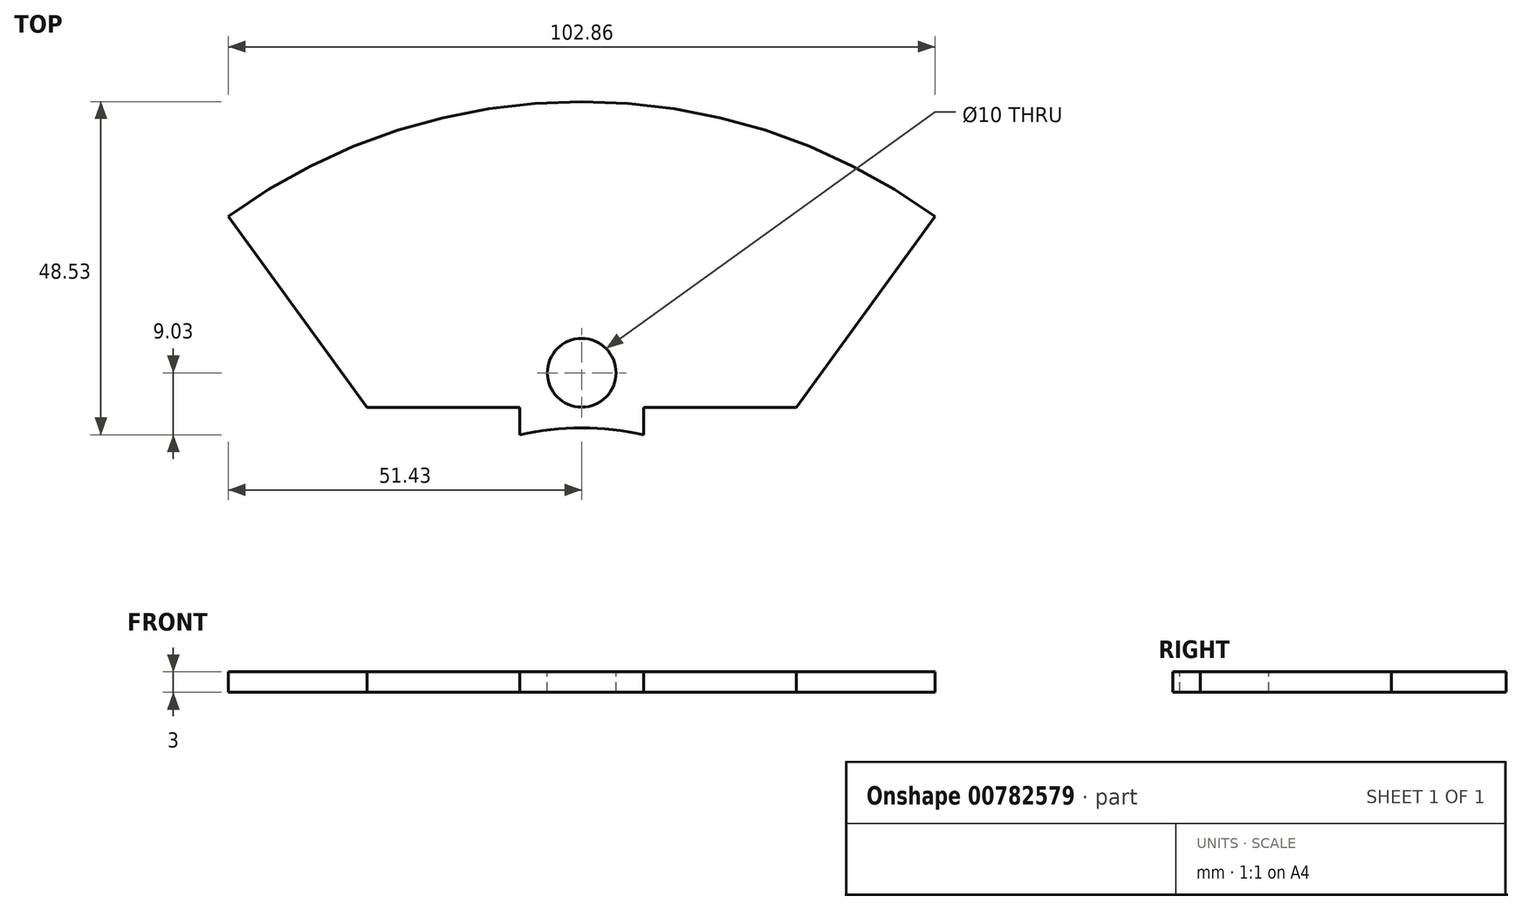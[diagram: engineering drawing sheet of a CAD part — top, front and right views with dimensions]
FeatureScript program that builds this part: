
annotation { "Feature Type Name" : "Feature", "Feature Type Description" : "" }
export const myFeature = defineFeature(function(context is Context, id is Id, definition is map)
    precondition{}
    {
        {
            var Q0;
            Q0=qCreatedBy(makeId("Top.planeOp"),FACE);
            var sketch = newSketch(context, id + "F0", { "sketchPlane" : qUnion([Q0])});
            skArc(sketch, "E0", {"start": v(51.43, 70.79) * mm, "mid": v(0, 87.5) * mm, "end": v(-51.43, 70.79) * mm});
            skLineSegment(sketch, "E1", {"start": v(0, 0) * mm, "end": v(104.27, 0) * mm, "construction": true});
            skLineSegment(sketch, "E2", {"start": v(0, 0) * mm, "end": v(-103.94, 0) * mm, "construction": true});
            skLineSegment(sketch, "E3", {"start": v(0, 0) * mm, "end": v(0, 97.04) * mm, "construction": true});
            skLineSegment(sketch, "E4", {"start": v(0, 0) * mm, "end": v(0, -125.2) * mm, "construction": true});
            skLineSegment(sketch, "E5", {"start": v(0, 0) * mm, "end": v(51.43, 70.79) * mm});
            skLineSegment(sketch, "E6.MirrorCS", {"start": v(0, 0) * mm, "end": v(-51.43, 70.79) * mm});
            skSolve(sketch);
        }
        {
            var Q0;
            Q0=makeQuery(id+"F0.imprint","IMPRINT",FACE,{"disambiguationData":[TD([[makeQuery(id+"F0.imprint","IMPRINT",EDGE,{"derivedFrom":sQuery(id+"F0.wireOp",EDGE,"E0")}),1.0]])]});
            extrude(context, id + "F1", {"entities" : qUnion([Q0]), "depth" : 3 * mm, "offsetDistance" : 25 * mm});
        }
        {
            var Q0;
            Q0=makeQuery(id+"F1.opExtrude","CAP_FACE",FACE,{"disambiguationData":[OSD([sQuery(id+"F0.wireOp",EDGE,"E0"),sQuery(id+"F0.wireOp",EDGE,"E5"),sQuery(id+"F0.wireOp",EDGE,"E6.MirrorCS")])],"isStart":false});
            var sketch = newSketch(context, id + "F2", { "sketchPlane" : qUnion([Q0])});
            skCircle(sketch, "E7", {"center": v(0, 0) * mm, "radius": 40 * mm});
            skSolve(sketch);
        }
        {
            var Q0;
            {var subQ0=sQuery(id+"F2.wireOp",EDGE,"E7");var subQ1=makeQuery(id+"F1.opExtrude","CAP_EDGE",EDGE,{"disambiguationData":[OSD([sQuery(id+"F0.wireOp",EDGE,"E5")])],"isStart":false});var subQ2=makeQuery(id+"F2.imprint","INTERSECT",VERTEX,{"derivedFrom":[subQ1,subQ0]});Q0=makeQuery(id+"F2.imprint","IMPRINT",FACE,{"disambiguationData":[TD([[makeQuery(id+"F2.imprint","IMPRINT",EDGE,{"disambiguationData":[TD([[subQ2,-1.0]])],"derivedFrom":subQ0}),1.0]])]});}
            extrude(context, id + "F3", {"entities" : qUnion([Q0]), "operationType" : NewBodyOperationType.REMOVE, "endBound" : BoundingType.THROUGH_ALL, "oppositeDirection" : true, "depth" : 25 * mm, "offsetDistance" : 25 * mm});
        }
        {
            var Q0;
            Q0=makeQuery(id+"F1.opExtrude","CAP_FACE",FACE,{"disambiguationData":[OSD([sQuery(id+"F0.wireOp",EDGE,"E0"),sQuery(id+"F0.wireOp",EDGE,"E5"),sQuery(id+"F0.wireOp",EDGE,"E6.MirrorCS")])],"isStart":false});
            var sketch = newSketch(context, id + "F4", { "sketchPlane" : qUnion([Q0])});
            skCircle(sketch, "E8", {"center": v(0, 0) * mm, "radius": 55 * mm, "construction": true});
            skCircle(sketch, "E9", {"center": v(0, 48) * mm, "radius": 5 * mm});
            skSolve(sketch);
        }
        {
            var Q0;
            Q0=makeQuery(id+"F4.imprint","IMPRINT",FACE,{"disambiguationData":[TD([[makeQuery(id+"F4.imprint","IMPRINT",EDGE,{"derivedFrom":sQuery(id+"F4.wireOp",EDGE,"E9")}),1.0]])]});
            extrude(context, id + "F5", {"entities" : qUnion([Q0]), "operationType" : NewBodyOperationType.REMOVE, "endBound" : BoundingType.THROUGH_ALL, "oppositeDirection" : true, "depth" : 25 * mm, "offsetDistance" : 25 * mm});
        }
        {
            var Q0;
            Q0=makeQuery(id+"F1.opExtrude","CAP_FACE",FACE,{"disambiguationData":[OSD([sQuery(id+"F0.wireOp",EDGE,"E0"),sQuery(id+"F0.wireOp",EDGE,"E5"),sQuery(id+"F0.wireOp",EDGE,"E6.MirrorCS")])],"isStart":false});
            var sketch = newSketch(context, id + "F6", { "sketchPlane" : qUnion([Q0])});
            skCircle(sketch, "E10", {"center": v(0, 0) * mm, "radius": 55 * mm, "construction": true});
            skLineSegment(sketch, "E11", {"start": v(0, 31.85) * mm, "end": v(0, 58.19) * mm, "construction": true});
            skLineSegment(sketch, "E12", {"start": v(0, 53) * mm, "end": v(9, 53) * mm, "construction": true});
            skLineSegment(sketch, "E13", {"start": v(0, 53) * mm, "end": v(-9, 53) * mm, "construction": true});
            skLineSegment(sketch, "E14", {"start": v(-9, 53) * mm, "end": v(-9, 35.22) * mm, "construction": true});
            skLineSegment(sketch, "E15", {"start": v(9, 53) * mm, "end": v(9, 33.37) * mm, "construction": true});
            skLineSegment(sketch, "E16.bottom", {"start": v(-9, 38.97) * mm, "end": v(-31.45, 38.97) * mm});
            skLineSegment(sketch, "E16.top", {"start": v(-9, 29.02) * mm, "end": v(-31.45, 29.02) * mm});
            skLineSegment(sketch, "E16.left", {"start": v(-9, 38.97) * mm, "end": v(-9, 29.02) * mm});
            skLineSegment(sketch, "E16.right", {"start": v(-31.45, 38.97) * mm, "end": v(-31.45, 29.02) * mm});
            skLineSegment(sketch, "E17.bottom", {"start": v(9, 38.97) * mm, "end": v(31.12, 38.97) * mm});
            skLineSegment(sketch, "E17.top", {"start": v(9, 26.95) * mm, "end": v(31.12, 26.95) * mm});
            skLineSegment(sketch, "E17.left", {"start": v(9, 38.97) * mm, "end": v(9, 26.95) * mm});
            skLineSegment(sketch, "E17.right", {"start": v(31.12, 38.97) * mm, "end": v(31.12, 26.95) * mm});
            skSolve(sketch);
        }
        {
            var Q0;
            {var subQ1=makeQuery(id+"F3.boolean.opBoolean","COPY",EDGE,{"derivedFrom":makeQuery(id+"F3.opExtrude","CAP_EDGE",EDGE,{"disambiguationData":[OSD([sQuery(id+"F2.wireOp",EDGE,"E7")])],"isStart":true})});var subQ3=makeQuery(id+"F1.opExtrude","CAP_EDGE",EDGE,{"disambiguationData":[OSD([sQuery(id+"F0.wireOp",EDGE,"E6.MirrorCS")])],"isStart":false});var subQ5=makeQuery(id+"F6.imprint","INTERSECT",VERTEX,{"derivedFrom":[subQ1,subQ3]});Q0=makeQuery(id+"F6.imprint","IMPRINT",FACE,{"disambiguationData":[TD([[makeQuery(id+"F6.imprint","IMPRINT",EDGE,{"disambiguationData":[TD([[subQ5,-1.0]])],"derivedFrom":subQ3}),-1.0]])]});}
            var Q1;
            {var subQ1=makeQuery(id+"F3.boolean.opBoolean","COPY",EDGE,{"derivedFrom":makeQuery(id+"F3.opExtrude","CAP_EDGE",EDGE,{"disambiguationData":[OSD([sQuery(id+"F2.wireOp",EDGE,"E7")])],"isStart":true})});var subQ3=makeQuery(id+"F1.opExtrude","CAP_EDGE",EDGE,{"disambiguationData":[OSD([sQuery(id+"F0.wireOp",EDGE,"E5")])],"isStart":false});var subQ5=makeQuery(id+"F6.imprint","INTERSECT",VERTEX,{"derivedFrom":[subQ1,subQ3]});Q1=makeQuery(id+"F6.imprint","IMPRINT",FACE,{"disambiguationData":[TD([[makeQuery(id+"F6.imprint","IMPRINT",EDGE,{"disambiguationData":[TD([[subQ5,-1.0]])],"derivedFrom":subQ3}),1.0]])]});}
            extrude(context, id + "F7", {"entities" : qUnion([Q0, Q1]), "operationType" : NewBodyOperationType.REMOVE, "endBound" : BoundingType.THROUGH_ALL, "oppositeDirection" : true, "depth" : 25 * mm, "offsetDistance" : 25 * mm});
        }
        {
            var Q0;
            Q0=makeQuery(id+"F1.opExtrude","CAP_FACE",FACE,{"disambiguationData":[OSD([sQuery(id+"F0.wireOp",EDGE,"E0"),sQuery(id+"F0.wireOp",EDGE,"E5"),sQuery(id+"F0.wireOp",EDGE,"E6.MirrorCS")])],"isStart":false});
            var sketch = newSketch(context, id + "F8", { "sketchPlane" : qUnion([Q0])});
            skLineSegment(sketch, "E18", {"start": v(9, 38.97) * mm, "end": v(9, 45.6) * mm, "construction": true});
            skLineSegment(sketch, "E19", {"start": v(-9, 38.97) * mm, "end": v(-9, 42.97) * mm, "construction": true});
            skLineSegment(sketch, "E20.bottom", {"start": v(-9, 38.97) * mm, "end": v(-37.3, 38.97) * mm});
            skLineSegment(sketch, "E20.top", {"start": v(-9, 42.97) * mm, "end": v(-37.3, 42.97) * mm});
            skLineSegment(sketch, "E20.left", {"start": v(-9, 38.97) * mm, "end": v(-9, 42.97) * mm});
            skLineSegment(sketch, "E20.right", {"start": v(-37.3, 38.97) * mm, "end": v(-37.3, 42.97) * mm});
            skLineSegment(sketch, "E21.bottom", {"start": v(9, 38.97) * mm, "end": v(49.27, 38.97) * mm});
            skLineSegment(sketch, "E21.top", {"start": v(9, 42.97) * mm, "end": v(49.27, 42.97) * mm});
            skLineSegment(sketch, "E21.left", {"start": v(9, 38.97) * mm, "end": v(9, 42.97) * mm});
            skLineSegment(sketch, "E21.right", {"start": v(49.27, 38.97) * mm, "end": v(49.27, 42.97) * mm});
            skSolve(sketch);
        }
        {
            var Q0;
            {var subQ0=sQuery(id+"F8.wireOp",EDGE,"E20.left");Q0=makeQuery(id+"F8.imprint","IMPRINT",FACE,{"disambiguationData":[TD([[makeQuery(id+"F8.imprint","IMPRINT",EDGE,{"derivedFrom":subQ0}),1.0]])]});}
            var Q1;
            {var subQ0=sQuery(id+"F8.wireOp",EDGE,"E21.left");Q1=makeQuery(id+"F8.imprint","IMPRINT",FACE,{"disambiguationData":[TD([[makeQuery(id+"F8.imprint","IMPRINT",EDGE,{"derivedFrom":subQ0}),-1.0]])]});}
            extrude(context, id + "F9", {"entities" : qUnion([Q0, Q1]), "operationType" : NewBodyOperationType.REMOVE, "endBound" : BoundingType.THROUGH_ALL, "oppositeDirection" : true, "depth" : 25 * mm, "offsetDistance" : 25 * mm});
        }
    });
